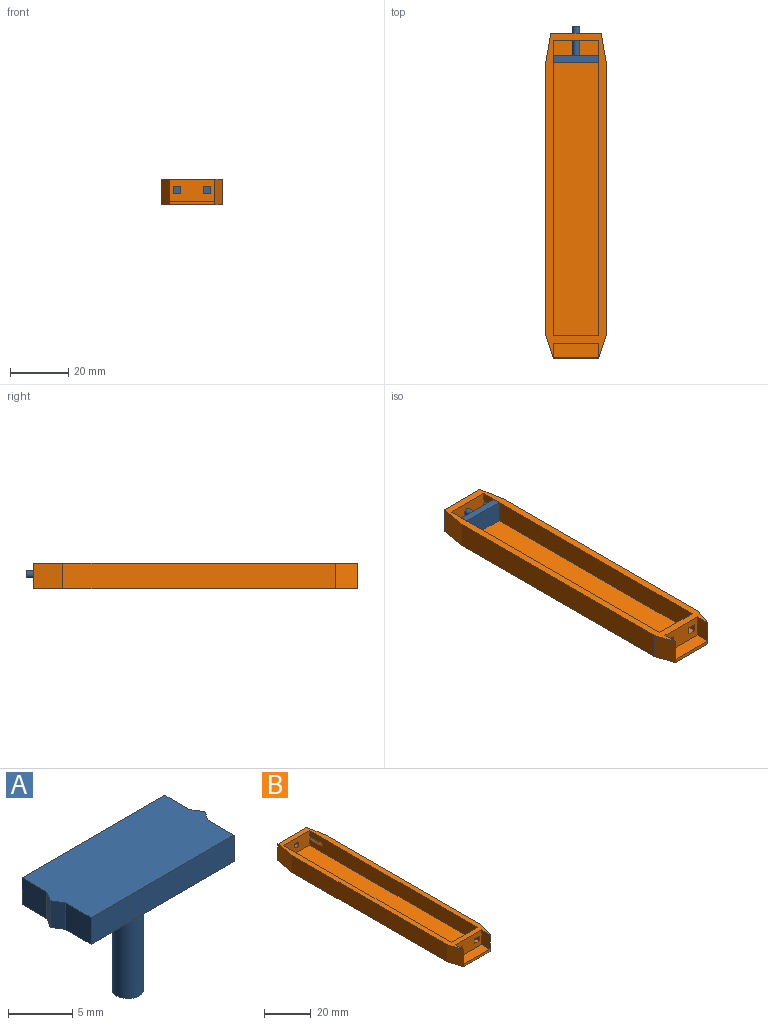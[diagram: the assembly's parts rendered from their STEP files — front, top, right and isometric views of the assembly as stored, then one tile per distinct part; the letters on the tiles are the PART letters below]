
ASSEMBLY  parts=2 mates=1
PART A: 14 faces, bbox 17x7.6x12.7 mm
  f0: plane 2.84x2.54mm, normal (1,0,0), area 7.2mm2, adj f1,f9,f10,f11
  f1: plane 2.54x1.02mm, normal (0.85,-0.53,0), area 3mm2, adj f0,f2,f10,f11
  f2: plane 2.54x1.02mm, normal (0.85,0.53,0), area 3mm2, adj f1,f3,f10,f11
  f3: plane 2.75x2.54mm, normal (1,0,0), area 7mm2, adj f2,f4,f10,f11
  f4: plane 15.75x2.54mm, normal (0,1,0), area 40mm2, adj f3,f5,f10,f11
  f5: plane 2.75x2.54mm, normal (-1,0,0), area 7mm2, adj f4,f6,f10,f11
  f6: plane 2.54x1.02mm, normal (-0.85,0.53,0), area 3mm2, adj f5,f7,f10,f11
  f7: plane 2.54x1.02mm, normal (-0.85,-0.53,0), area 3mm2, adj f6,f8,f10,f11
  f8: plane 2.84x2.54mm, normal (-1,0,0), area 7.2mm2, adj f7,f9,f10,f11
  f9: plane 15.75x2.54mm, normal (0,-1,0), area 40mm2, adj f0,f8,f10,f11
  f10: plane 17.02x7.62mm, normal (0,0,1), area 121.3mm2, adj f0,f1,f2,f3,f4,f5,f6,f7
  f11: plane 17.02x7.62mm, normal (0,0,-1), area 116.4mm2, adj f0,f1,f2,f3,f4,f5,f6,f7
  f12: cylinder r=1.24mm len=10.16mm, axis (0,0,1), area 79.5mm2, adj f11,f13
  f13: plane 2.49x2.49mm, normal (0,0,-1), area 4.9mm2, adj f12
PART B: 34 faces, bbox 20.8x111.8x8.9 mm
  f0: plane 101.6x7.62mm, normal (-1,0,0), area 758.7mm2, adj f2,f12,f14,f16,f30,f31,f32
  f1: plane 101.6x7.62mm, normal (1,0,0), area 758.7mm2, adj f2,f12,f14,f16,f27,f28,f29
  f2: plane 17.02x7.62mm, normal (0,-1,0), area 116.2mm2, adj f0,f1,f12,f16,f28,f29,f31,f32
  f3: plane 7.62x5.09mm, normal (-1,0,0), area 38.7mm2, adj f4,f12,f13,f15
  f4: plane 8.89x7.62mm, normal (0.95,-0.32,0), area 71.4mm2, adj f3,f5,f12,f17,f18
  f5: plane 93.98x8.89mm, normal (1,0,0), area 835.5mm2, adj f4,f6,f12,f18
  f6: plane 10.16x8.89mm, normal (0.99,0.17,0), area 91.6mm2, adj f5,f7,f12,f18
  f7: plane 17.36x8.89mm, normal (0,1,0), area 149.2mm2, adj f6,f8,f12,f18,f33
  f8: plane 10.16x8.89mm, normal (-0.99,0.17,0), area 91.6mm2, adj f7,f9,f12,f18
  f9: plane 93.98x8.89mm, normal (-1,0,0), area 835.5mm2, adj f8,f10,f12,f18
  f10: plane 8.89x7.62mm, normal (-0.95,-0.32,0), area 71.4mm2, adj f9,f11,f12,f17,f18
  f11: plane 7.62x5.09mm, normal (1,0,0), area 38.7mm2, adj f10,f12,f13,f15
  f12: plane 111.76x20.83mm, normal (0,0,1), area 610.8mm2, adj f0,f1,f2,f3,f4,f5,f6,f7
  f13: plane 15.75x5.09mm, normal (0,0,1), area 80.1mm2, adj f3,f11,f15,f17
  f14: plane 15.75x7.62mm, normal (0,1,0), area 107.1mm2, adj f0,f1,f12,f16,f19,f20,f21,f22
  f15: plane 15.75x7.62mm, normal (0,-1,0), area 107.1mm2, adj f3,f11,f12,f13,f19,f20,f21,f22
  f16: plane 101.6x15.75mm, normal (0,0,1), area 1599.9mm2, adj f0,f1,f2,f14
  f17: plane 15.75x1.27mm, normal (0,-1,0), area 20mm2, adj f4,f10,f13,f18
  f18: plane 111.76x20.83mm, normal (0,0,-1), area 2290.7mm2, adj f4,f5,f6,f7,f8,f9,f10,f17
  f19: plane 2.54x2.54mm, normal (-1,0,0), area 6.5mm2, adj f14,f15,f20,f22
  f20: plane 2.54x2.54mm, normal (0,0,-1), area 6.5mm2, adj f14,f15,f19,f21
  f21: plane 2.54x2.54mm, normal (1,0,0), area 6.5mm2, adj f14,f15,f20,f22
  f22: plane 2.54x2.54mm, normal (0,0,1), area 6.5mm2, adj f14,f15,f19,f21
  f23: plane 2.54x2.54mm, normal (1,0,0), area 6.5mm2, adj f14,f15,f24,f26
  f24: plane 2.54x2.54mm, normal (0,0,1), area 6.5mm2, adj f14,f15,f23,f25
  f25: plane 2.54x2.54mm, normal (-1,0,0), area 6.5mm2, adj f14,f15,f24,f26
  f26: plane 2.54x2.54mm, normal (0,0,-1), area 6.5mm2, adj f14,f15,f23,f25
  f27: plane 2.03x0.64mm, normal (0,1,0), area 0.6mm2, adj f1,f28,f29
  f28: plane 7.62x1.02mm, normal (0.85,0,0.53), area 9.1mm2, adj f1,f2,f27,f29
  f29: plane 7.62x1.02mm, normal (0.85,0,-0.53), area 9.1mm2, adj f1,f2,f27,f28
  f30: plane 2.03x0.64mm, normal (0,1,0), area 0.6mm2, adj f0,f31,f32
  f31: plane 7.62x1.02mm, normal (-0.85,0,-0.53), area 9.1mm2, adj f0,f2,f30,f32
  f32: plane 7.62x1.02mm, normal (-0.85,0,0.53), area 9.1mm2, adj f0,f2,f30,f31
  f33: cylinder r=1.27mm len=2.54mm, axis (0,1,0), area 20.3mm2, adj f2,f7
PLACE A rot(axis=(1,0,0),90deg) t=(-11.44,42.6,1.95)mm
PLACE B t=(-11.44,-6.93,-1.82)mm fixed
MATE slider A.f10 <-> B.f27  axis (0,-1,0) through (-19.95,40.06,1.99)mm
